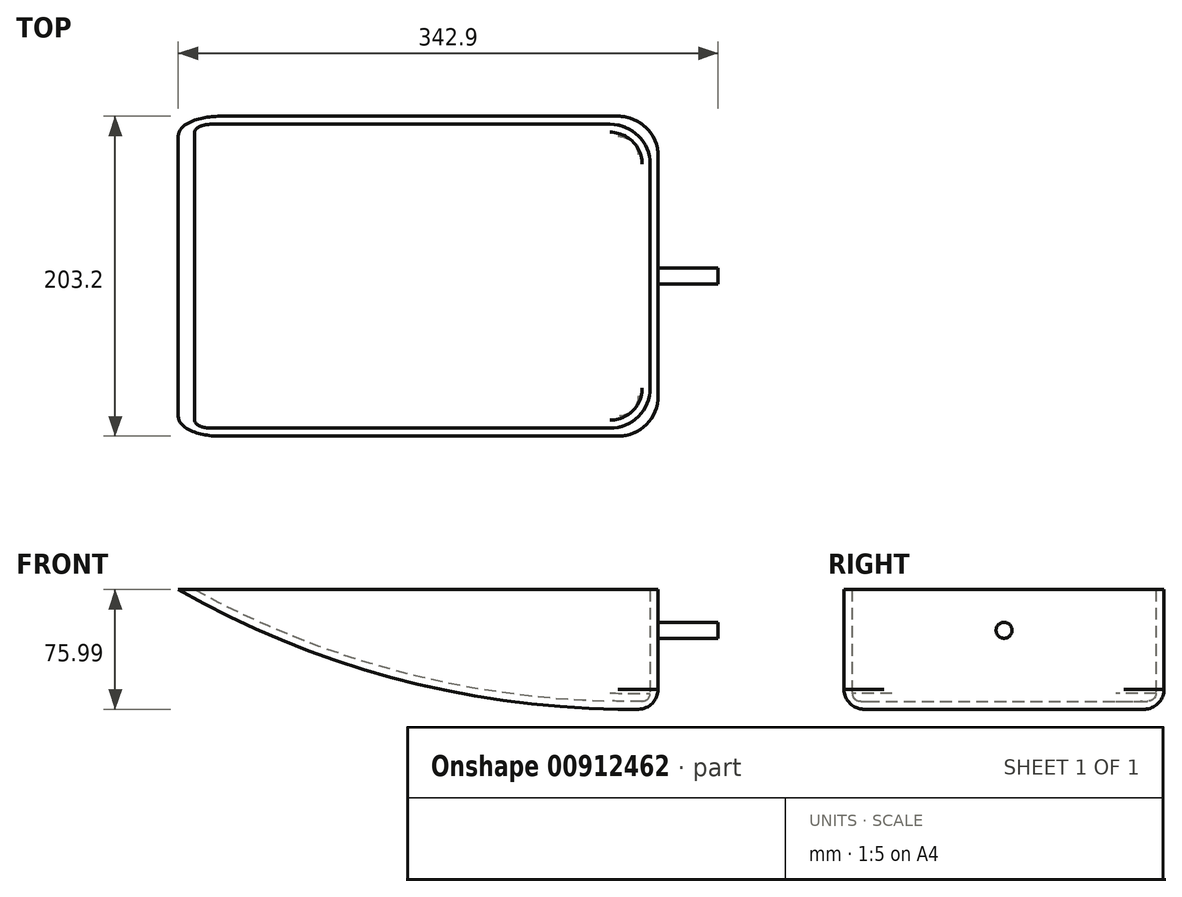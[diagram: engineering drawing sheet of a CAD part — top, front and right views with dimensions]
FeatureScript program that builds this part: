
annotation { "Feature Type Name" : "Feature", "Feature Type Description" : "" }
export const myFeature = defineFeature(function(context is Context, id is Id, definition is map)
    precondition{}
    {
        {
            var Q0;
            Q0=qCreatedBy(makeId("Right.planeOp"),FACE);
            var sketch = newSketch(context, id + "F0", { "sketchPlane" : qUnion([Q0])});
            skLineSegment(sketch, "E0", {"start": v(-101.6, 20.32) * mm, "end": v(-101.6, -37.28) * mm});
            skLineSegment(sketch, "E1.MirrorCS", {"start": v(101.6, 20.32) * mm, "end": v(101.6, -37.28) * mm});
            skLineSegment(sketch, "E2", {"start": v(-88.9, -49.98) * mm, "end": v(88.9, -49.98) * mm});
            skPoint(sketch, "E3.visualSharp", {"position": v(-101.6, -49.98) * mm});
            skArc(sketch, "E3.filletArc", {"start": v(-101.6, -37.28) * mm, "mid": v(-97.88, -46.26) * mm, "end": v(-88.9, -49.98) * mm});
            skPoint(sketch, "E4.visualSharp", {"position": v(101.6, -49.98) * mm});
            skArc(sketch, "E4.filletArc", {"start": v(88.9, -49.98) * mm, "mid": v(97.88, -46.26) * mm, "end": v(101.6, -37.28) * mm});
            skLineSegment(sketch, "E5", {"start": v(-96.52, 25.4) * mm, "end": v(96.52, 25.4) * mm});
            skPoint(sketch, "E6.visualSharp", {"position": v(-101.6, 25.4) * mm});
            skArc(sketch, "E6.filletArc", {"start": v(-96.52, 25.4) * mm, "mid": v(-100.11, 23.91) * mm, "end": v(-101.6, 20.32) * mm});
            skPoint(sketch, "E7.visualSharp", {"position": v(101.6, 25.4) * mm});
            skArc(sketch, "E7.filletArc", {"start": v(101.6, 20.32) * mm, "mid": v(100.11, 23.91) * mm, "end": v(96.52, 25.4) * mm});
            skCircle(sketch, "E8", {"center": v(0, 0) * mm, "radius": 5.08 * mm});
            skSolve(sketch);
        }
        {
            var Q0;
            Q0=qCreatedBy(makeId("Front.planeOp"),FACE);
            var sketch = newSketch(context, id + "F1", { "sketchPlane" : qUnion([Q0])});
            skLineSegment(sketch, "E9", {"start": v(0, 25.85) * mm, "end": v(-304.8, 25.85) * mm});
            skArc(sketch, "E10", {"start": v(-304.8, 25.85) * mm, "mid": v(-157.6, -32.98) * mm, "end": v(0, -49.88) * mm});
            skLineSegment(sketch, "E11", {"start": v(0, 25.85) * mm, "end": v(0, -49.88) * mm});
            skSolve(sketch);
        }
        {
            var Q0;
            Q0=makeQuery(id+"F1.imprint","IMPRINT",FACE,{"disambiguationData":[TD([[makeQuery(id+"F1.imprint","IMPRINT",EDGE,{"derivedFrom":sQuery(id+"F1.wireOp",EDGE,"E9")}),1.0]])]});
            extrude(context, id + "F2", {"entities" : qUnion([Q0]), "endBound" : BoundingType.SYMMETRIC, "depth" : 203.2 * mm, "offsetDistance" : 25.4 * mm});
        }
        {
            var Q0;
            Q0=makeQuery(id+"F2.opExtrude","SWEPT_FACE",FACE,{"disambiguationData":[OSD([sQuery(id+"F1.wireOp",EDGE,"E9")])]});
            shell(context, id + "F3", {"entities" : qUnion([Q0]), "thickness" : 5.08 * mm});
        }
        {
            var Q0;
            Q0=makeQuery(id+"F0.imprint","IMPRINT",FACE,{"disambiguationData":[TD([[makeQuery(id+"F0.imprint","IMPRINT",EDGE,{"derivedFrom":sQuery(id+"F0.wireOp",EDGE,"E8")}),1.0]])]});
            extrude(context, id + "F4", {"entities" : qUnion([Q0]), "operationType" : NewBodyOperationType.ADD, "depth" : 38.1 * mm, "offsetDistance" : 25.4 * mm});
        }
        {
            var Q0;
            Q0=makeQuery(id+"F2.opExtrude","CAP_EDGE",EDGE,{"disambiguationData":[OSD([sQuery(id+"F1.wireOp",EDGE,"E11")])],"isStart":false});
            var Q1;
            {var subQ0=sQuery(id+"F1.wireOp",EDGE,"E11");Q1=makeQuery(id+"F3.opShell","OFFSET_EDGE",EDGE,{"disambiguationData":[OSD([subQ0]),TDD([makeQuery(id+"F2.opExtrude","CAP_EDGE",EDGE,{"disambiguationData":[OSD([subQ0])],"isStart":false})])]});}
            var Q2;
            {var subQ0=sQuery(id+"F1.wireOp",EDGE,"E11");Q2=makeQuery(id+"F3.opShell","OFFSET_EDGE",EDGE,{"disambiguationData":[OSD([subQ0]),TDD([makeQuery(id+"F2.opExtrude","CAP_EDGE",EDGE,{"disambiguationData":[OSD([subQ0])],"isStart":true})])]});}
            var Q3;
            Q3=makeQuery(id+"F2.opExtrude","CAP_EDGE",EDGE,{"disambiguationData":[OSD([sQuery(id+"F1.wireOp",EDGE,"E11")])],"isStart":true});
            fillet(context, id + "F5", {"entities" : qUnion([Q0, Q1, Q2, Q3]), "radius" : 25.4 * mm, "tangentPropagation" : true, "allowEdgeOverflow" : false});
        }
        {
            var Q0;
            Q0=makeQuery(id+"F5.opFillet","BLEND_EDGE",EDGE,{"blendedFrom":[makeQuery(id+"F2.opExtrude","CAP_EDGE",EDGE,{"disambiguationData":[OSD([sQuery(id+"F1.wireOp",EDGE,"E11")])],"isStart":false}),makeQuery(id+"F2.opExtrude","SWEPT_FACE",FACE,{"disambiguationData":[OSD([sQuery(id+"F1.wireOp",EDGE,"E10")])]})],"blendedInto":[makeQuery(id+"F2.opExtrude","SWEPT_FACE",FACE,{"disambiguationData":[OSD([sQuery(id+"F1.wireOp",EDGE,"E10")])]})]});
            fillet(context, id + "F6", {"entities" : qUnion([Q0]), "radius" : 12.7 * mm, "tangentPropagation" : true, "allowEdgeOverflow" : false});
        }
        {
            var Q0;
            {var subQ0=sQuery(id+"F1.wireOp",EDGE,"E11");Q0=makeQuery(id+"F5.opFillet","BLEND_EDGE",EDGE,{"blendedFrom":[makeQuery(id+"F3.opShell","OFFSET_EDGE",EDGE,{"disambiguationData":[OSD([subQ0]),TDD([makeQuery(id+"F2.opExtrude","CAP_EDGE",EDGE,{"disambiguationData":[OSD([subQ0])],"isStart":true})])]}),makeQuery(id+"F3.opShell","OFFSET_FACE",FACE,{"disambiguationData":[OSD([sQuery(id+"F1.wireOp",EDGE,"E10")])]})],"blendedInto":[makeQuery(id+"F3.opShell","OFFSET_FACE",FACE,{"disambiguationData":[OSD([sQuery(id+"F1.wireOp",EDGE,"E10")])]})]});}
            fillet(context, id + "F7", {"entities" : qUnion([Q0]), "radius" : 5.08 * mm, "tangentPropagation" : true, "allowEdgeOverflow" : false});
        }
    });
